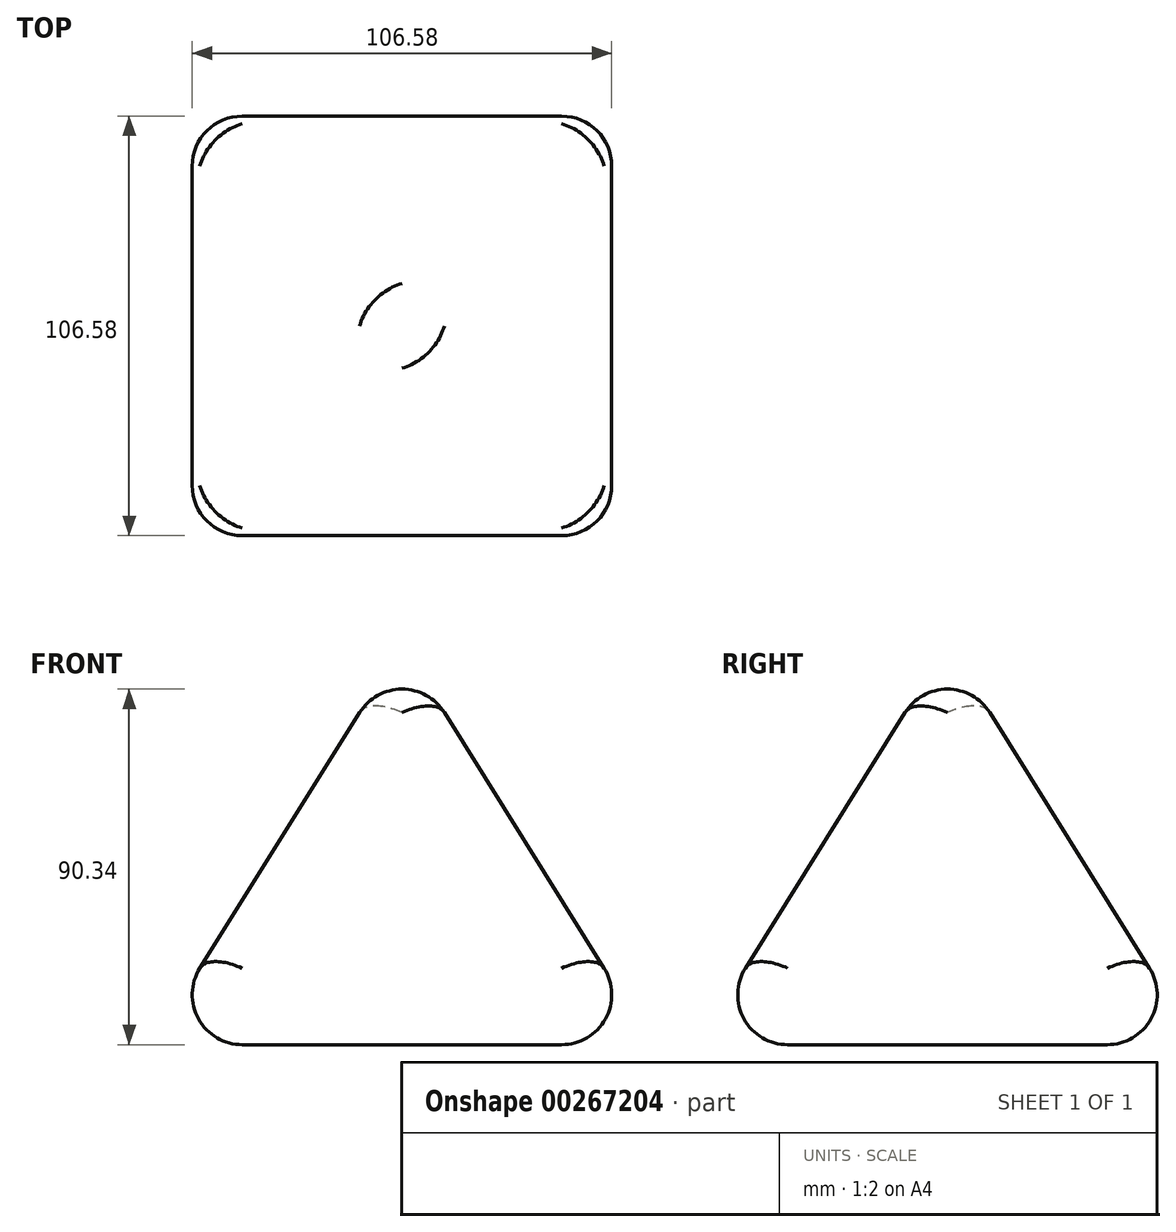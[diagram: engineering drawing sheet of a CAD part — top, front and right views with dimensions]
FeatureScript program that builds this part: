
annotation { "Feature Type Name" : "Feature", "Feature Type Description" : "" }
export const myFeature = defineFeature(function(context is Context, id is Id, definition is map)
    precondition{}
    {
        {
            var Q0;
            Q0=qCreatedBy(makeId("Top.planeOp"),FACE);
            var sketch = newSketch(context, id + "F0", { "sketchPlane" : qUnion([Q0])});
            skLineSegment(sketch, "E0.bottom", {"start": v(-63.5, 63.5) * mm, "end": v(63.5, 63.5) * mm});
            skLineSegment(sketch, "E0.top", {"start": v(-63.5, -63.5) * mm, "end": v(63.5, -63.5) * mm});
            skLineSegment(sketch, "E0.left", {"start": v(-63.5, 63.5) * mm, "end": v(-63.5, -63.5) * mm});
            skLineSegment(sketch, "E0.right", {"start": v(63.5, 63.5) * mm, "end": v(63.5, -63.5) * mm});
            skPoint(sketch, "E0.middle", {"position": v(0, 0) * mm});
            skSolve(sketch);
        }
        {
            var Q0;
            Q0=qCreatedBy(makeId("Top.planeOp"),FACE);
            cPlane(context, id + "F1", {"entities" : qUnion([Q0]), "cplaneType" : CPlaneType.OFFSET, "offset" : 101.6 * mm, "width" : 152.4 * mm, "height" : 152.4 * mm});
        }
        {
            var Q0;
            Q0=qCreatedBy(id+"F1.planeOp",FACE);
            var sketch = newSketch(context, id + "F2", { "sketchPlane" : qUnion([Q0])});
            skPoint(sketch, "E1", {"position": v(0, 0) * mm});
            skSolve(sketch);
        }
        {
            var Q0;
            Q0=sQuery(id+"F2.wireOp",VERTEX,"E1");
            var Q1;
            Q1=makeQuery(id+"F0.imprint","IMPRINT",FACE,{"disambiguationData":[TD([[makeQuery(id+"F0.imprint","IMPRINT",EDGE,{"derivedFrom":sQuery(id+"F0.wireOp",EDGE,"E0.bottom")}),-1.0]])]});
            loft(context, id + "F3", {"sheetProfilesArray" : [{ "sheetProfileEntities" : qUnion([Q0]) }, { "sheetProfileEntities" : qUnion([Q1]) }]});
        }
        {
            var Q0;
            Q0=makeQuery(id+"F3.opLoft","SWEPT_EDGE",EDGE,{"disambiguationData":[OSD([sQuery(id+"F0.wireOp",EDGE,"E0.top"),sQuery(id+"F0.wireOp",EDGE,"E0.left"),sQuery(id+"F2.wireOp",VERTEX,"E1")])]});
            var Q1;
            Q1=makeQuery(id+"F3.opLoft","SWEPT_EDGE",EDGE,{"disambiguationData":[OSD([sQuery(id+"F0.wireOp",EDGE,"E0.top"),sQuery(id+"F0.wireOp",EDGE,"E0.right"),sQuery(id+"F2.wireOp",VERTEX,"E1")])]});
            var Q2;
            Q2=makeQuery(id+"F3.opLoft","SWEPT_EDGE",EDGE,{"disambiguationData":[OSD([sQuery(id+"F0.wireOp",EDGE,"E0.bottom"),sQuery(id+"F0.wireOp",EDGE,"E0.right"),sQuery(id+"F2.wireOp",VERTEX,"E1")])]});
            var Q3;
            Q3=makeQuery(id+"F3.opLoft","SWEPT_EDGE",EDGE,{"disambiguationData":[OSD([sQuery(id+"F0.wireOp",EDGE,"E0.bottom"),sQuery(id+"F0.wireOp",EDGE,"E0.left"),sQuery(id+"F2.wireOp",VERTEX,"E1")])]});
            var Q4;
            Q4=makeQuery(id+"F3.opLoft","SWEPT_FACE",FACE,{"disambiguationData":[OSD([sQuery(id+"F0.wireOp",EDGE,"E0.bottom"),sQuery(id+"F0.wireOp",EDGE,"E0.left"),sQuery(id+"F0.wireOp",EDGE,"E0.right")])]});
            var Q5;
            Q5=makeQuery(id+"F3.opLoft","SWEPT_FACE",FACE,{"disambiguationData":[OSD([sQuery(id+"F0.wireOp",EDGE,"E0.bottom"),sQuery(id+"F0.wireOp",EDGE,"E0.top"),sQuery(id+"F0.wireOp",EDGE,"E0.left")])]});
            var Q6;
            Q6=makeQuery(id+"F3.opLoft","SWEPT_FACE",FACE,{"disambiguationData":[OSD([sQuery(id+"F0.wireOp",EDGE,"E0.top"),sQuery(id+"F0.wireOp",EDGE,"E0.left"),sQuery(id+"F0.wireOp",EDGE,"E0.right")])]});
            var Q7;
            Q7=makeQuery(id+"F3.opLoft","SWEPT_FACE",FACE,{"disambiguationData":[OSD([sQuery(id+"F0.wireOp",EDGE,"E0.bottom"),sQuery(id+"F0.wireOp",EDGE,"E0.top"),sQuery(id+"F0.wireOp",EDGE,"E0.right")])]});
            fillet(context, id + "F4", {"entities" : qUnion([Q0, Q1, Q2, Q3, Q4, Q5, Q6, Q7]), "radius" : 12.7 * mm, "tangentPropagation" : true, "allowEdgeOverflow" : false});
        }
    });
